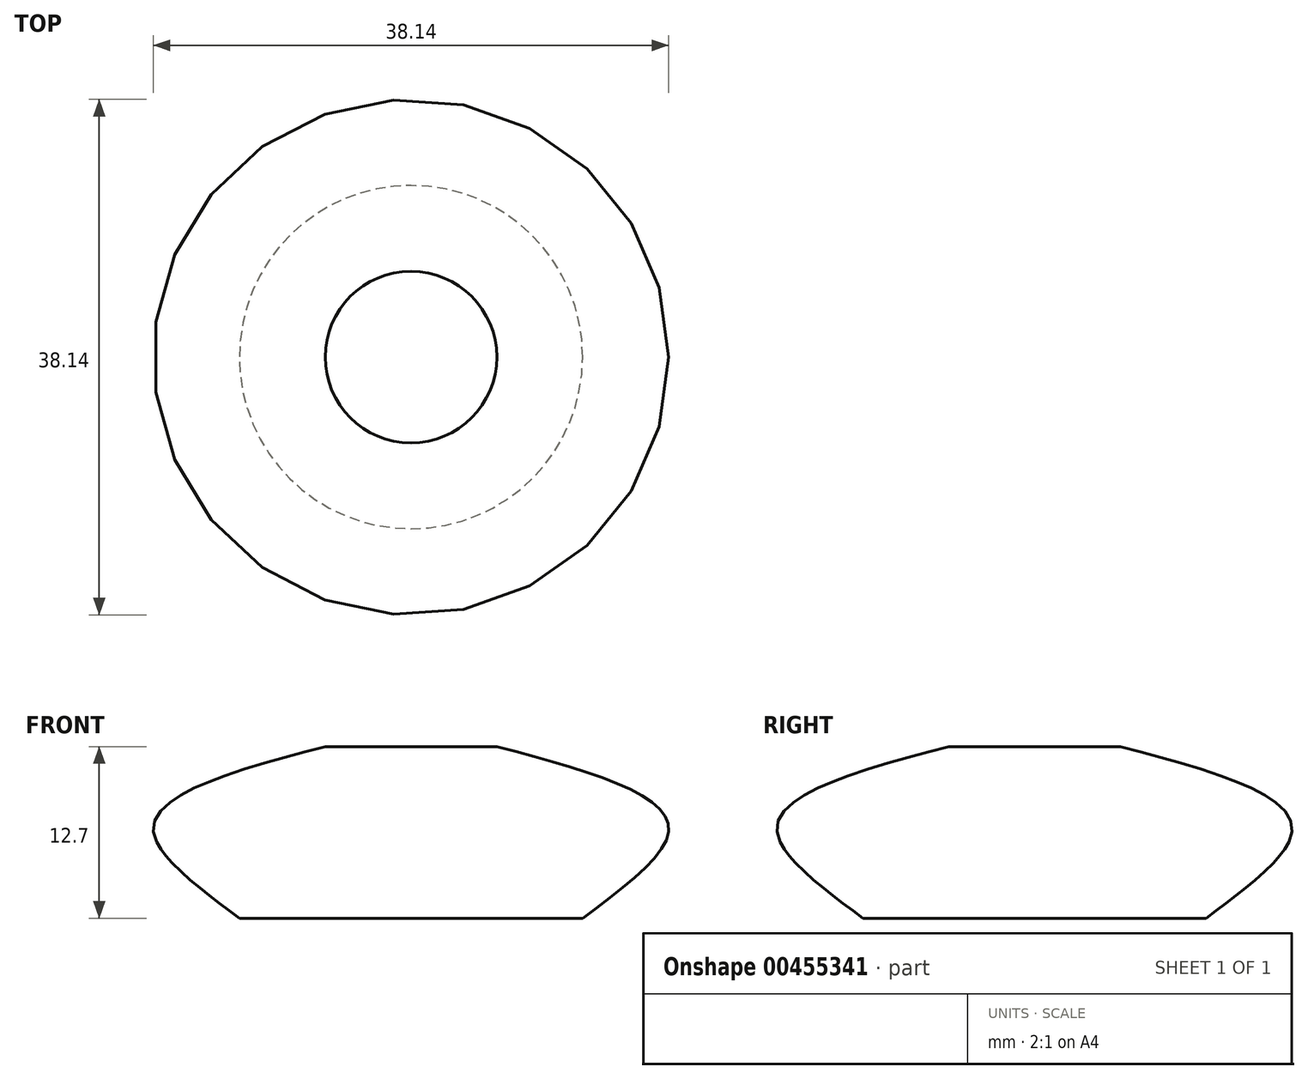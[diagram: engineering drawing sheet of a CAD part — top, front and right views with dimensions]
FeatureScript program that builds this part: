
annotation { "Feature Type Name" : "Feature", "Feature Type Description" : "" }
export const myFeature = defineFeature(function(context is Context, id is Id, definition is map)
    precondition{}
    {
        {
            var Q0;
            Q0=qCreatedBy(makeId("Top.planeOp"),FACE);
            var sketch = newSketch(context, id + "F0", { "sketchPlane" : qUnion([Q0])});
            skCircle(sketch, "E0", {"center": v(0, 0) * mm, "radius": 12.7 * mm});
            skSolve(sketch);
        }
        {
            var Q0;
            Q0=qCreatedBy(makeId("Top.planeOp"),FACE);
            cPlane(context, id + "F1", {"entities" : qUnion([Q0]), "cplaneType" : CPlaneType.OFFSET, "offset" : 6.35 * mm, "width" : 152.4 * mm, "height" : 152.4 * mm});
        }
        {
            var Q0;
            Q0=qCreatedBy(id+"F1.planeOp",FACE);
            var sketch = newSketch(context, id + "F2", { "sketchPlane" : qUnion([Q0])});
            skCircle(sketch, "E1", {"center": v(0, 0) * mm, "radius": 19.05 * mm});
            skSolve(sketch);
        }
        {
            var Q0;
            Q0=qCreatedBy(makeId("Top.planeOp"),FACE);
            cPlane(context, id + "F3", {"entities" : qUnion([Q0]), "cplaneType" : CPlaneType.OFFSET, "offset" : 12.7 * mm, "width" : 152.4 * mm, "height" : 152.4 * mm});
        }
        {
            var Q0;
            Q0=qCreatedBy(id+"F3.planeOp",FACE);
            var sketch = newSketch(context, id + "F4", { "sketchPlane" : qUnion([Q0])});
            skCircle(sketch, "E2", {"center": v(0, 0) * mm, "radius": 6.35 * mm});
            skSolve(sketch);
        }
        {
            var Q0;
            Q0=makeQuery(id+"F0.imprint","IMPRINT",FACE,{"disambiguationData":[TD([[makeQuery(id+"F0.imprint","IMPRINT",EDGE,{"derivedFrom":sQuery(id+"F0.wireOp",EDGE,"E0")}),1.0]])]});
            var Q1;
            Q1=makeQuery(id+"F2.imprint","IMPRINT",FACE,{"disambiguationData":[TD([[makeQuery(id+"F2.imprint","IMPRINT",EDGE,{"derivedFrom":sQuery(id+"F2.wireOp",EDGE,"E1")}),1.0]])]});
            var Q2;
            Q2=makeQuery(id+"F4.imprint","IMPRINT",FACE,{"disambiguationData":[TD([[makeQuery(id+"F4.imprint","IMPRINT",EDGE,{"derivedFrom":sQuery(id+"F4.wireOp",EDGE,"E2")}),1.0]])]});
            loft(context, id + "F5", {"sheetProfilesArray" : [{ "sheetProfileEntities" : qUnion([Q0]) }, { "sheetProfileEntities" : qUnion([Q1]) }, { "sheetProfileEntities" : qUnion([Q2]) }]});
        }
    });
